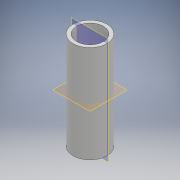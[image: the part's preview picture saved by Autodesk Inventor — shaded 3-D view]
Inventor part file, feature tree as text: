
AUTODESK INVENTOR PART (.ipt)
format: ipt  version: 2017 (Build 210142000, 142)  size: 96,256 bytes
history: native  units: mm
features: extrude x1, sketch x1
ambient origin geometry x8: Origin, YZ Plane, XZ Plane, XY Plane, X Axis, Y Axis, Z Axis, Center Point
bodies: Solid1 (feature_tree)
feature tree (2):
  extrude  "Extrusion1"  Depth=75.0mm
  sketch  "Sketch1"  dims[d0=26.0mm d1=2.7mm d2=75.0mm d3=0.0mm]
